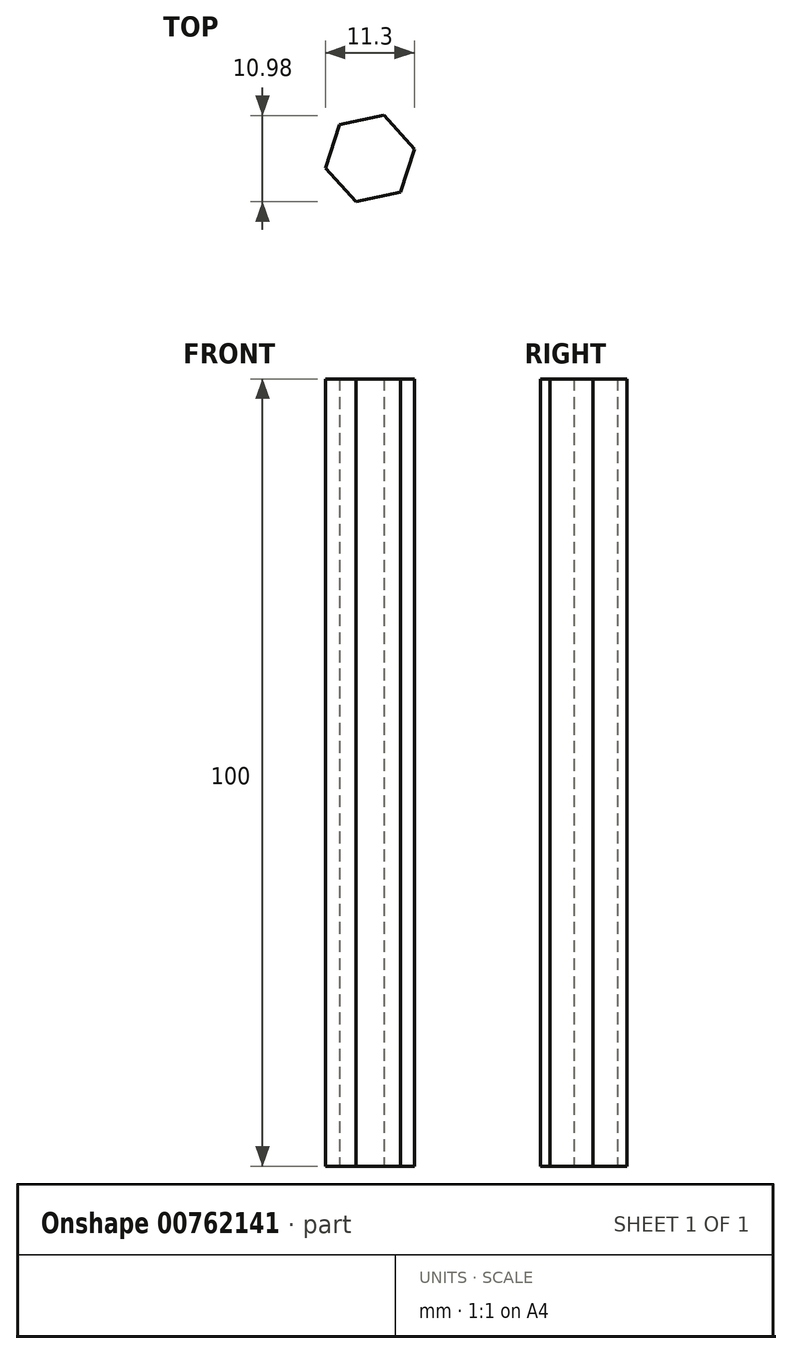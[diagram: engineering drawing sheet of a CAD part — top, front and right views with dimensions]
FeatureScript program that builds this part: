
annotation { "Feature Type Name" : "Feature", "Feature Type Description" : "" }
export const myFeature = defineFeature(function(context is Context, id is Id, definition is map)
    precondition{}
    {
        {
            var Q0;
            Q0=qCreatedBy(makeId("Top.planeOp"),FACE);
            var sketch = newSketch(context, id + "F0", { "sketchPlane" : qUnion([Q0])});
            skCircle(sketch, "E0.cCircle", {"center": v(0, 0) * mm, "radius": 5 * mm, "construction": true});
            skLineSegment(sketch, "E0.0", {"start": v(1.78, 5.5) * mm, "end": v(5.65, 1.2) * mm});
            skLineSegment(sketch, "E0.1", {"start": v(5.65, 1.2) * mm, "end": v(3.87, -4.29) * mm});
            skLineSegment(sketch, "E0.2", {"start": v(3.87, -4.29) * mm, "end": v(-1.78, -5.5) * mm});
            skLineSegment(sketch, "E0.3", {"start": v(-1.78, -5.5) * mm, "end": v(-5.65, -1.2) * mm});
            skLineSegment(sketch, "E0.4", {"start": v(-5.65, -1.2) * mm, "end": v(-3.87, 4.29) * mm});
            skLineSegment(sketch, "E0.5", {"start": v(-3.87, 4.29) * mm, "end": v(1.78, 5.5) * mm});
            skPoint(sketch, "E0.0.midPoint", {"position": v(3.71, 3.35) * mm});
            skSolve(sketch);
        }
        {
            var Q0;
            Q0 = qSketchRegion(id + "F0", true);
            extrude(context, id + "F1", {"entities" : qUnion([Q0]), "depth" : 100 * mm, "offsetDistance" : 25 * mm});
        }
    });
